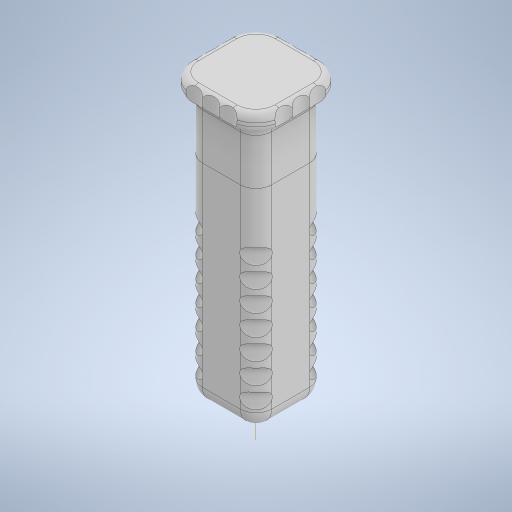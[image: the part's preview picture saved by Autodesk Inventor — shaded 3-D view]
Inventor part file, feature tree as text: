
AUTODESK INVENTOR PART (.ipt)
format: ipt  version: 2023 (Build 270158030, 158C)  size: 905,728 bytes
history: native  units: mm
features: sketch x8, extrude x7, fillet x4, other x3, projected_geometry x3, plane x2, revolve x1
ambient origin geometry x8: Origin, YZ Plane, XZ Plane, XY Plane, X Axis, Y Axis, Z Axis, Center Point
bodies: Body1 (feature_tree), Body2 (feature_tree)
feature tree (28):
  other  "body-tube"
  extrude  "Extrusion1"  Depth=2.5mm
  extrude  "Extrusion2"  Depth=2.0mm
  extrude  "Extrusion3"  Depth=4.5mm
  plane  "Work Plane1"
  extrude  "Extrusion4"  Depth=7.75mm
  fillet  "Fillet2"  Radius=7.75mm
  fillet  "Fillet3"  Radius=2.0mm
  extrude  "Extrusion5"  Depth=16.0mm
  extrude  "Extrusion6"  Depth=2.5mm
  fillet  "Fillet4"  Radius=8.9mm
  fillet  "Fillet5"  Radius=8.9mm
  plane  "Work Plane2"
  other  "Work Axis1"
  revolve  "Revolution1"  [1 undecoded]
  extrude  "Extrusion7"  Depth=3.0mm
  sketch  "Sketch1"  dims[d0=15.5mm d1=15.5mm d2=2.5mm]
  sketch  "Sketch2"  dims[d3=2.0mm d4=2.0mm d5=2.0mm]
  sketch  "Sketch3"  dims[d6=2.0mm d7=4.5mm]
  projected_geometry  "Projected Loop1"
  sketch  "Sketch4"  dims[d8=4.5mm d9=7.75mm d10=7.75mm d11=16.3mm d12=2.0mm]
  sketch  "Sketch5"  dims[d13=16.0mm d14=16.0mm]
  projected_geometry  "Projected Loop2"
  other  "lid"
  sketch  "Sketch6"  dims[d17=2.5mm d18=2.5mm d19=8.9mm d20=8.9mm]
  projected_geometry  "Projected Loop3"
  sketch  "Sketch8"  dims[d21=2.0mm d22=73.0mm d23=0.0mm]
  sketch  "Sketch9"  dims[d24=3.0mm d25=0.0mm d26=1.0mm d27=1.0mm d28=1.0mm d29=1.0mm d30=3.5mm d31=3.5mm d32=15.0mm d33=0.0mm d34=0.0mm d35=65.0mm d36=0.0mm d37=1.570796mm d39=2.0mm d40=5.0mm d41=15.5mm d42=0.0mm d43=5.0mm d44=0.0mm d45=2.0mm d46=2.5mm d47=6.0mm d48=6.0mm d49=6.0mm d50=6.0mm d51=6.0mm d52=5.0mm d53=3.0mm d54=360.0deg d55=5.0mm d56=5.0mm d57=8.0mm d61=5.0mm d62=40.0mm d64=360.0deg d66=0.0mm d67=-0.174533mm d68=8.0mm d69=8.0mm d70=8.9mm d71=8.9mm d72=6.0mm d73=5.0mm d74=5.0mm d75=3.0mm d76=3.0mm d77=3.0mm d78=3.0mm d79=7.5mm d80=4.5mm d81=7.5mm d82=6.0mm d83=6.0mm d84=6.0mm]
note: 1 required parameter value undecoded (feature->parameter linkage not recoverable at this tier; creation-order binding heuristic only, values carry confidence <= 0.55)
